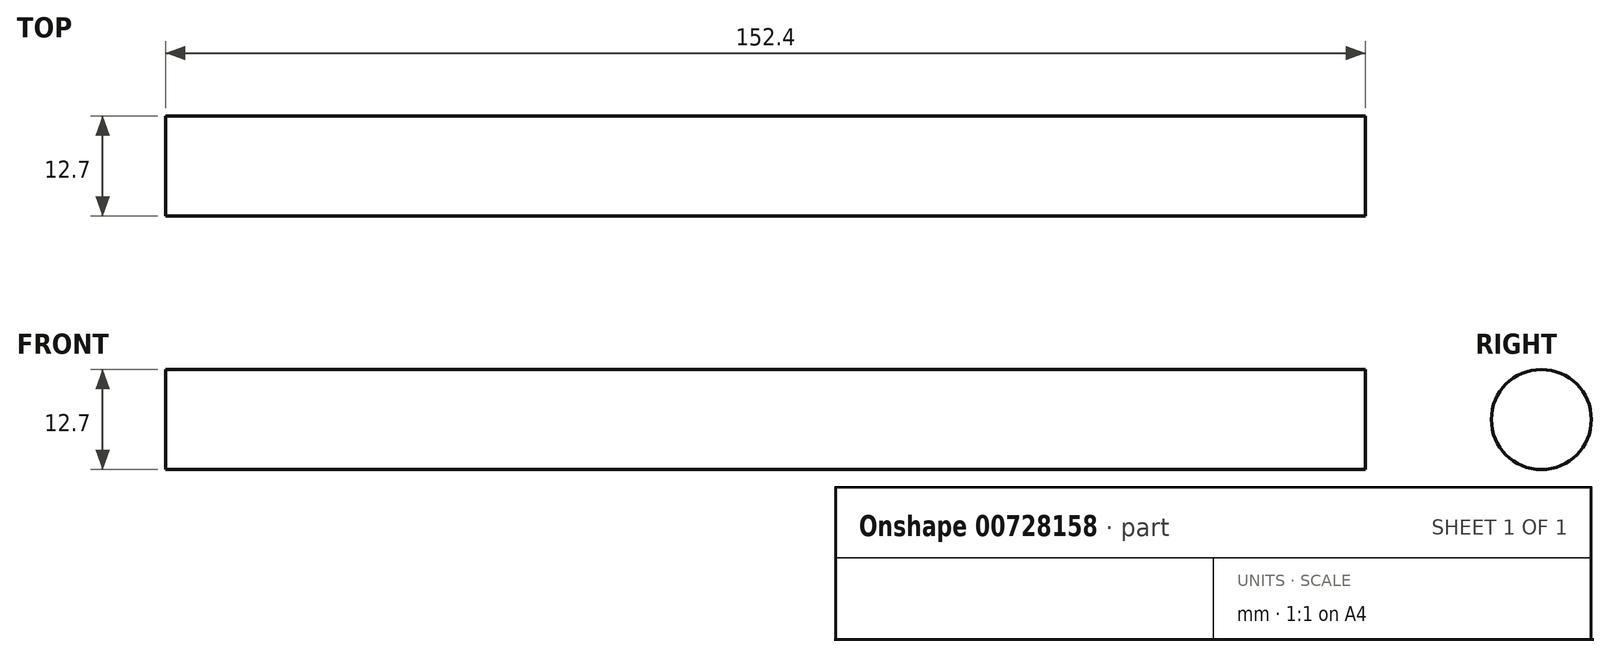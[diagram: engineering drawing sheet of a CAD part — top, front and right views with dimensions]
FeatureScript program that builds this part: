
annotation { "Feature Type Name" : "Feature", "Feature Type Description" : "" }
export const myFeature = defineFeature(function(context is Context, id is Id, definition is map)
    precondition{}
    {
        {
            var Q0;
            Q0=qCreatedBy(makeId("Right.planeOp"),FACE);
            var sketch = newSketch(context, id + "F0", { "sketchPlane" : qUnion([Q0])});
            skCircle(sketch, "E0", {"center": v(0, 0) * mm, "radius": 6.35 * mm});
            skSolve(sketch);
        }
        {
            var Q0;
            Q0=makeQuery(id+"F0.imprint","IMPRINT",FACE,{"disambiguationData":[TD([[makeQuery(id+"F0.imprint","IMPRINT",EDGE,{"derivedFrom":sQuery(id+"F0.wireOp",EDGE,"E0")}),1.0]])]});
            extrude(context, id + "F1", {"entities" : qUnion([Q0]), "depth" : 152.4 * mm, "offsetDistance" : 25.4 * mm});
        }
    });
